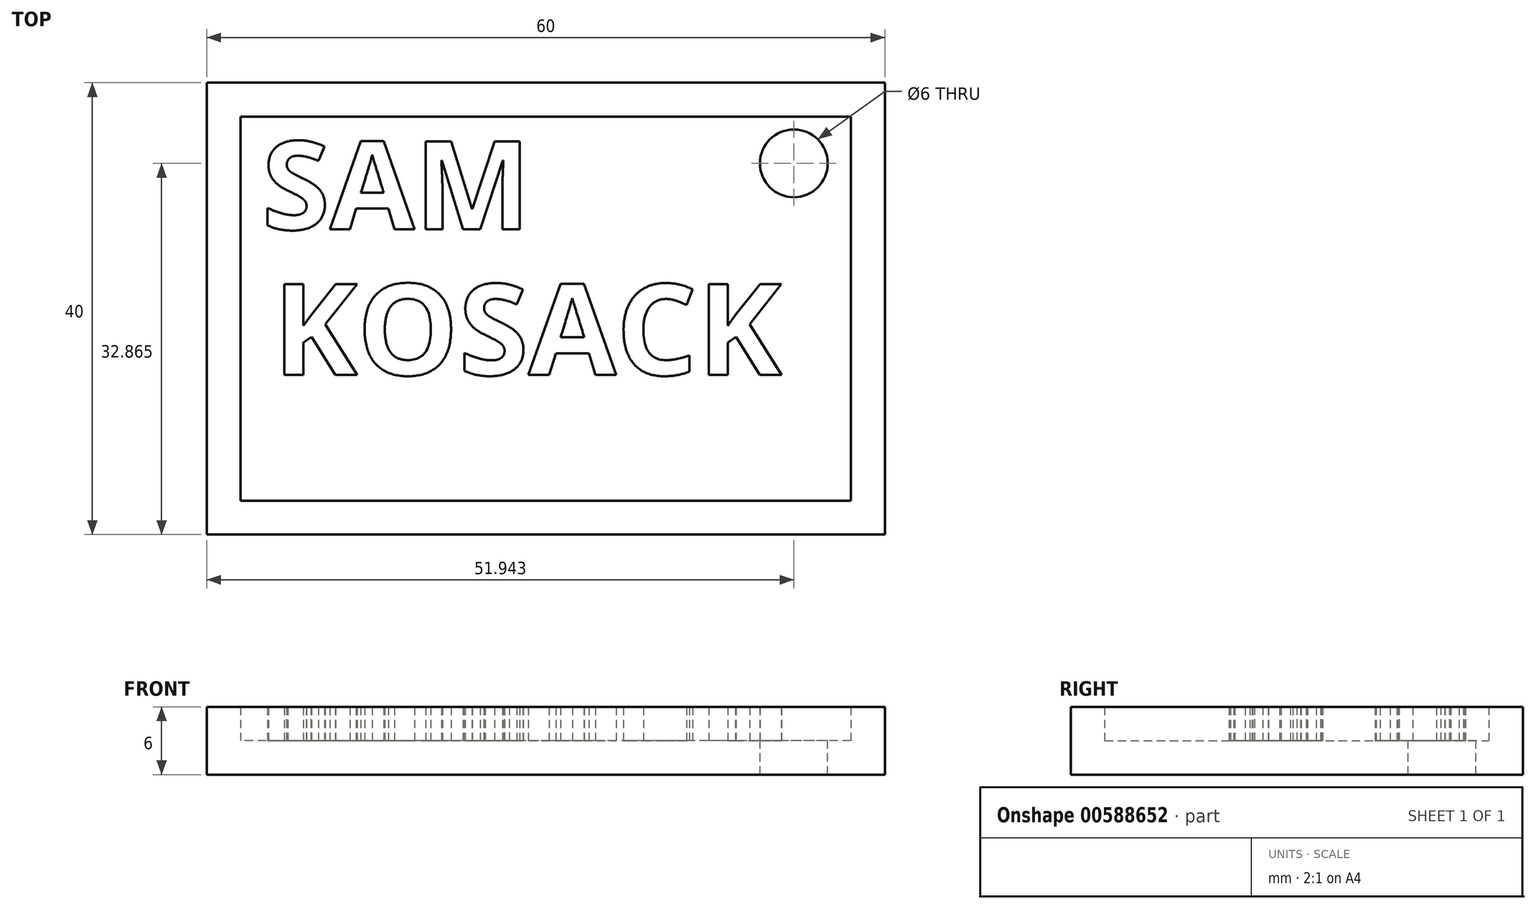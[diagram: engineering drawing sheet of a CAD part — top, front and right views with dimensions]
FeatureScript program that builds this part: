
annotation { "Feature Type Name" : "Feature", "Feature Type Description" : "" }
export const myFeature = defineFeature(function(context is Context, id is Id, definition is map)
    precondition{}
    {
        {
            var Q0;
            Q0=qCreatedBy(makeId("Top.planeOp"),FACE);
            var sketch = newSketch(context, id + "F0", { "sketchPlane" : qUnion([Q0])});
            skLineSegment(sketch, "E0.bottom", {"start": v(30, -20) * mm, "end": v(-30, -20) * mm});
            skLineSegment(sketch, "E0.top", {"start": v(30, 20) * mm, "end": v(-30, 20) * mm});
            skLineSegment(sketch, "E0.left", {"start": v(30, -20) * mm, "end": v(30, 20) * mm});
            skLineSegment(sketch, "E0.right", {"start": v(-30, -20) * mm, "end": v(-30, 20) * mm});
            skPoint(sketch, "E0.middle", {"position": v(0, 0) * mm});
            skSolve(sketch);
        }
        {
            var Q0;
            Q0=makeQuery(id+"F0.imprint","IMPRINT",FACE,{"disambiguationData":[TD([[makeQuery(id+"F0.imprint","IMPRINT",EDGE,{"derivedFrom":sQuery(id+"F0.wireOp",EDGE,"E0.bottom")}),-1.0]])]});
            extrude(context, id + "F1", {"entities" : qUnion([Q0]), "depth" : 6 * mm, "offsetDistance" : 25 * mm});
        }
        {
            var Q0;
            Q0=makeQuery(id+"F1.opExtrude","CAP_FACE",FACE,{"disambiguationData":[OSD([sQuery(id+"F0.wireOp",EDGE,"E0.bottom"),sQuery(id+"F0.wireOp",EDGE,"E0.top"),sQuery(id+"F0.wireOp",EDGE,"E0.left"),sQuery(id+"F0.wireOp",EDGE,"E0.right")])],"isStart":false});
            shell(context, id + "F2", {"entities" : qUnion([Q0]), "thickness" : 3 * mm});
        }
        {
            var Q0;
            Q0=makeQuery(id+"F2.opShell","OFFSET_FACE",FACE,{"disambiguationData":[OSD([sQuery(id+"F0.wireOp",EDGE,"E0.bottom"),sQuery(id+"F0.wireOp",EDGE,"E0.top"),sQuery(id+"F0.wireOp",EDGE,"E0.left"),sQuery(id+"F0.wireOp",EDGE,"E0.right")])]});
            var sketch = newSketch(context, id + "F3", { "sketchPlane" : qUnion([Q0])});
            skText(sketch, "E1", { "text": "SAM", "fontName": "OpenSans-Bold.ttf"});
            skText(sketch, "E2", { "text": "KOSACK", "fontName": "OpenSans-Bold.ttf"});
            const initialGuessF3  = {"E1": [-0.02513, 0.00702, 1, 0, 0.00785], "E2": [-0.02416, -0.00587, 1, 0, 0.0081]};
            skSetInitialGuess(sketch, initialGuessF3);
            skSolve(sketch);
        }
        {
            var Q0;
            Q0=makeQuery(id+"F3.imprint","IMPRINT",FACE,{"disambiguationData":[TD([[makeQuery(id+"F3.imprint","IMPRINT",EDGE,{"derivedFrom":sQuery(id+"F3.wireOp",EDGE,"E1.sketch_text.stroke-0")}),1.0]])]});
            var sketch = newSketch(context, id + "F4", { "sketchPlane" : qUnion([Q0])});
            skCircle(sketch, "E3", {"center": v(21.94, 12.86) * mm, "radius": 3.96 * mm});
            skSolve(sketch);
        }
        {
            var Q0;
            Q0=sQuery(id+"F4.wireOp",VERTEX,"E3.center");
            var Q1;
            Q1=makeQuery(id+"F1.opExtrude","SWEPT_BODY",BODY,{"disambiguationData":[OSD([sQuery(id+"F0.wireOp",EDGE,"E0.bottom"),sQuery(id+"F0.wireOp",EDGE,"E0.top"),sQuery(id+"F0.wireOp",EDGE,"E0.left"),sQuery(id+"F0.wireOp",EDGE,"E0.right")])]});
            hole(context, id + "F5", {"style" : HoleStyle.SIMPLE, "endStyle" : HoleEndStyle.THROUGH, "holeDiameter" : 6 * mm, "majorDiameter" : 5 * mm, "isTappedThrough" : true, "tappedDepth" : 12 * mm, "tapClearance" : 3, "locations" : qUnion([Q0]), "scope" : qUnion([Q1])});
        }
        {
            var Q0;
            Q0 = qSketchRegion(id + "F3", true);
            extrude(context, id + "F6", {"entities" : qUnion([Q0]), "operationType" : NewBodyOperationType.ADD, "depth" : 3 * mm, "offsetDistance" : 25 * mm});
        }
    });
